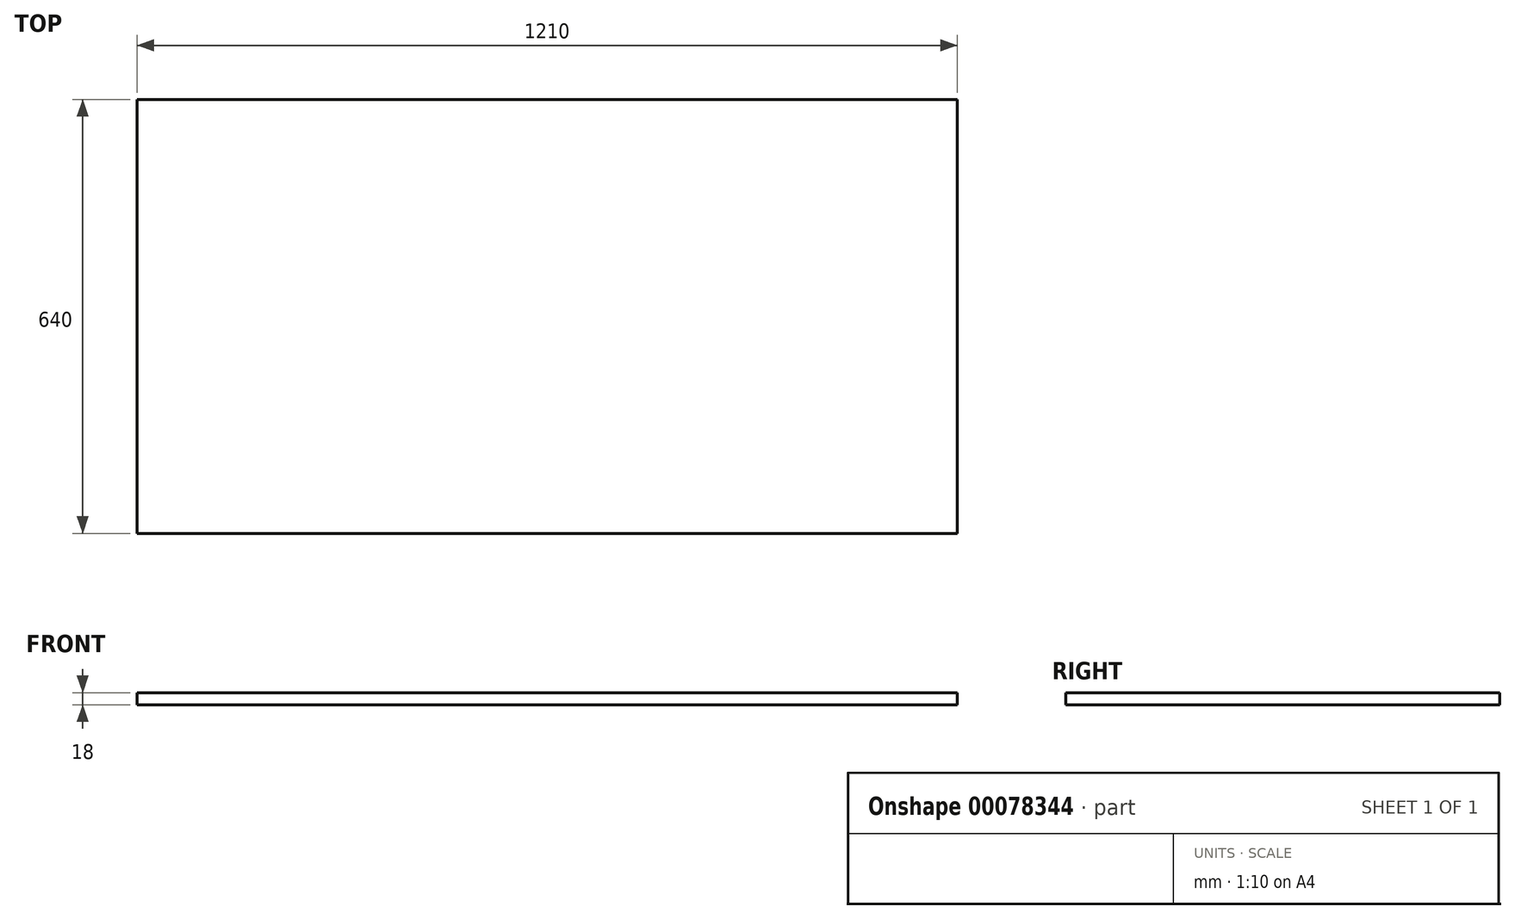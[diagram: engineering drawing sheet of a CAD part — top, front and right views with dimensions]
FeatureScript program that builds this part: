
annotation { "Feature Type Name" : "Feature", "Feature Type Description" : "" }
export const myFeature = defineFeature(function(context is Context, id is Id, definition is map)
    precondition{}
    {
        {
            var Q0;
            Q0=qCreatedBy(makeId("Top.planeOp"),FACE);
            var sketch = newSketch(context, id + "F0", { "sketchPlane" : qUnion([Q0])});
            skLineSegment(sketch, "E0.bottom", {"start": v(-605, 305.3) * mm, "end": v(605, 305.3) * mm});
            skLineSegment(sketch, "E0.top", {"start": v(-605, -334.7) * mm, "end": v(605, -334.7) * mm});
            skLineSegment(sketch, "E0.left", {"start": v(-605, 305.3) * mm, "end": v(-605, -334.7) * mm});
            skLineSegment(sketch, "E0.right", {"start": v(605, 305.3) * mm, "end": v(605, -334.7) * mm});
            skLineSegment(sketch, "E1", {"start": v(0, 0) * mm, "end": v(0, 259.24) * mm, "construction": true});
            skSolve(sketch);
        }
        {
            var Q0;
            Q0=makeQuery(id+"F0.imprint","IMPRINT",FACE,{"disambiguationData":[TD([[makeQuery(id+"F0.imprint","IMPRINT",EDGE,{"derivedFrom":sQuery(id+"F0.wireOp",EDGE,"E0.bottom")}),-1.0]])]});
            extrude(context, id + "F1", {"entities" : qUnion([Q0]), "depth" : 18 * mm});
        }
    });
